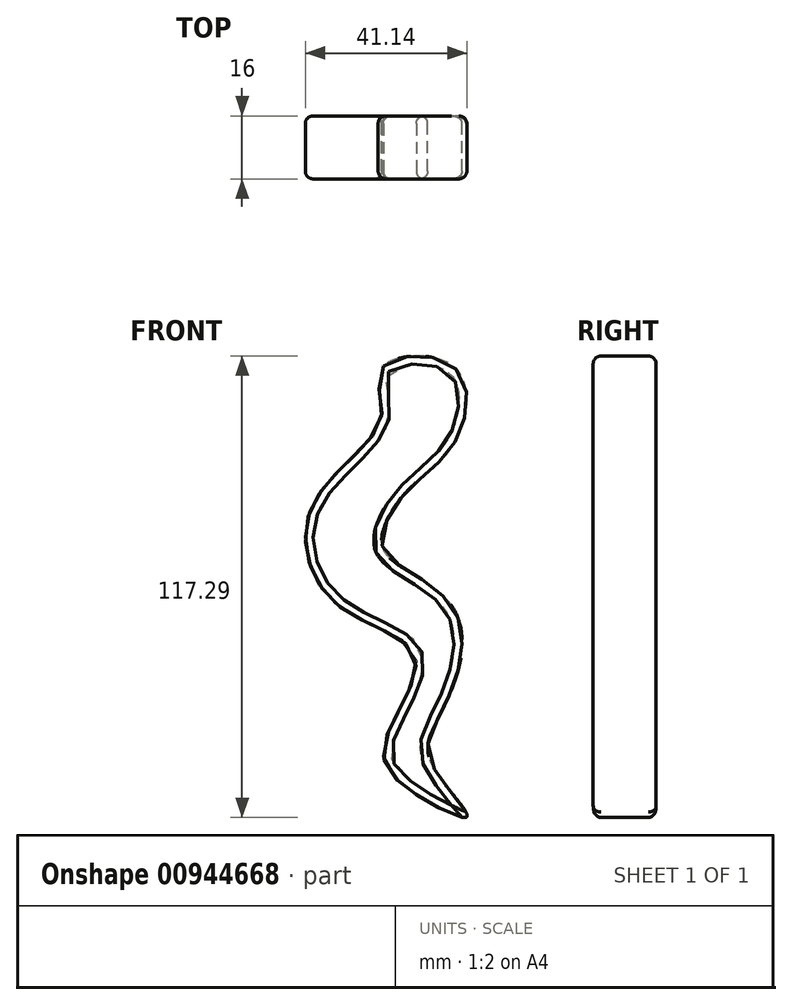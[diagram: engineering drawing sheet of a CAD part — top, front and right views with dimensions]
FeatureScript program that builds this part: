
annotation { "Feature Type Name" : "Feature", "Feature Type Description" : "" }
export const myFeature = defineFeature(function(context is Context, id is Id, definition is map)
    precondition{}
    {
        {
            var Q0;
            Q0=qCreatedBy(makeId("Front.planeOp"),FACE);
            var sketch = newSketch(context, id + "F0", { "sketchPlane" : qUnion([Q0])});
            skFitSpline(sketch, "E0", {"points": [v(0, 31.32) * mm, v(-17.43, 9.35) * mm, v(-11.4, -15.76) * mm, v(8.67, -29.18) * mm, v(1.07, -50.28) * mm, v(5.64, -61.9) * mm, v(21.8, -69.83) * mm, v(12.7, -56.13) * mm, v(14.02, -45.75) * mm, v(19.95, -30.98) * mm, v(17.88, -16.2) * mm, v(5, -6.28) * mm, v(0.12, -0.14) * mm, v(6.32, 12.65) * mm, v(18.97, 25.7) * mm, v(18.37, 44.57) * mm, v(0, 44.1) * mm, v(0, 31.32) * mm]});
            skSolve(sketch);
        }
        {
            var Q0;
            Q0=makeQuery(id+"F0.imprint","IMPRINT",FACE,{"disambiguationData":[TD([[makeQuery(id+"F0.imprint","IMPRINT",EDGE,{"derivedFrom":sQuery(id+"F0.wireOp",EDGE,"E0")}),1.0]])]});
            extrude(context, id + "F1", {"entities" : qUnion([Q0]), "depth" : 16 * mm, "offsetDistance" : 25.4 * mm});
        }
        {
            var Q0;
            Q0=makeQuery(id+"F1.opExtrude","CAP_FACE",FACE,{"disambiguationData":[OSD([sQuery(id+"F0.wireOp",EDGE,"E0")])],"isStart":true});
            var Q1;
            Q1=makeQuery(id+"F1.opExtrude","CAP_FACE",FACE,{"disambiguationData":[OSD([sQuery(id+"F0.wireOp",EDGE,"E0")])],"isStart":false});
            fillet(context, id + "F2", {"entities" : qUnion([Q0, Q1]), "radius" : 2 * mm, "tangentPropagation" : true, "allowEdgeOverflow" : false});
        }
    });
